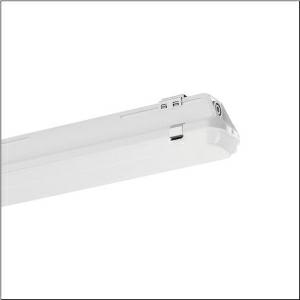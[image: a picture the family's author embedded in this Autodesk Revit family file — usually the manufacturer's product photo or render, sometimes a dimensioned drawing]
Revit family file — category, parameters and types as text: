
# Revit family: monsun_r__21_51fb207p460b_df7e
name_source: partatom
category: Lighting Fixtures
units: mm (PartAtom-declared; Revit-internal decimal feet)

## family parameters
Cut with Voids When Loaded = No
Host = Face
Light Source = No
Part Type = Normal
Room Calculation Point = No
Round Connector Dimension = Use Diameter
Shared = No

## types (1)
- Monsun® 21 (1 x LED, 5400 lm, 38 W, 4000K)
    Apparent Load = 38 VA
    CIE Flux Codes = 45 75 93 94 100
    Color Rendering = 80
    Color Temperature = 4000K
    Default Elevation = 1800 mm
    Description = Monsun® 21, damp-proof luminaire, chain hanger, primary optical cover: enclosure, of PC, light emission: direct distribution, primary light characteristic: symmetric, installation type: suspended mounting, surface-mounted, horizontal mounting, vertical mounting, LED, rated luminous flux: 5.400lm, luminous efficacy: 142lm/W, light colour: 840, colour temperature: 4000K, control gear: ECG, with terminal, 3-pole, max. 2.5mm², mains connection: 220..240V, AC, 50/60Hz, rated input power: 38W, housing, of glass-fibre reinforced polyester, uncoated, bright grey, length: 1.590mm, width: 90mm, height: 88mm, clip for enclosure, of stainless steel (V2A), ceiling mounting element, of stainless steel (V2A), chain hanger, of stainless steel (V2A), protection rating (complete): IP66, insulation class (complete): insulation class I (protective earthing), certification: CE, ENEC, VDE, UKCA, protection symbol: D, impact resistance: IK08, permissible operating ambient temperature: -25..+35°C, standard: EN 50419, EN 60598-2-1, corresponds to IFS (International Featured Standards) requirements for safety and quality in the food industry, for indoor or canopied outdoor use, no direct snow, no direct sun, no direct rain, packaging unit: 1 piece
    Height = 89 mm
    Lamp = 1 x LED
    Lamp Light Flux = 5400 lm
    Lamp Power = 38 W
    Lamp count = 1
    Length = 1590 mm
    Luminous efficacy = 142 lm/W
    Manufacturer = Siteco
    ModVariant = No
    Model = 51FB207P460B
    Mounting Place = Ceiling
    Mounting Type = Pendant
    Number of Poles = 1
    OnlyDefault = Yes
    Power Factor = 1
    Product Name = Monsun® 21
    Product group = damp-proof luminaire | ceiling pendant
    ProductGroupID = 908
    Protection Class = Protection class I
    Protection Degree = IP 66
    RLX_Detail_Level = 1
    RlxData = <blob elided: 88169 chars, md5=d30579af>
    Socket = socket
    Standby Power = 0 W
    System Light Flux = 5400 lm
    System Power = 38 W
    Type Comments = Product without accessories
    Type Image = l_1006717.jpg
    URL = http://relux.com
    VarID = ---
    Voltage = 0 V
    Weight = 0.00 kg
    Width = 90 mm

## geometry (parser evidence)
native form markers: Blend x4, Sweep x12
no freeform markers — native parametric forms only
